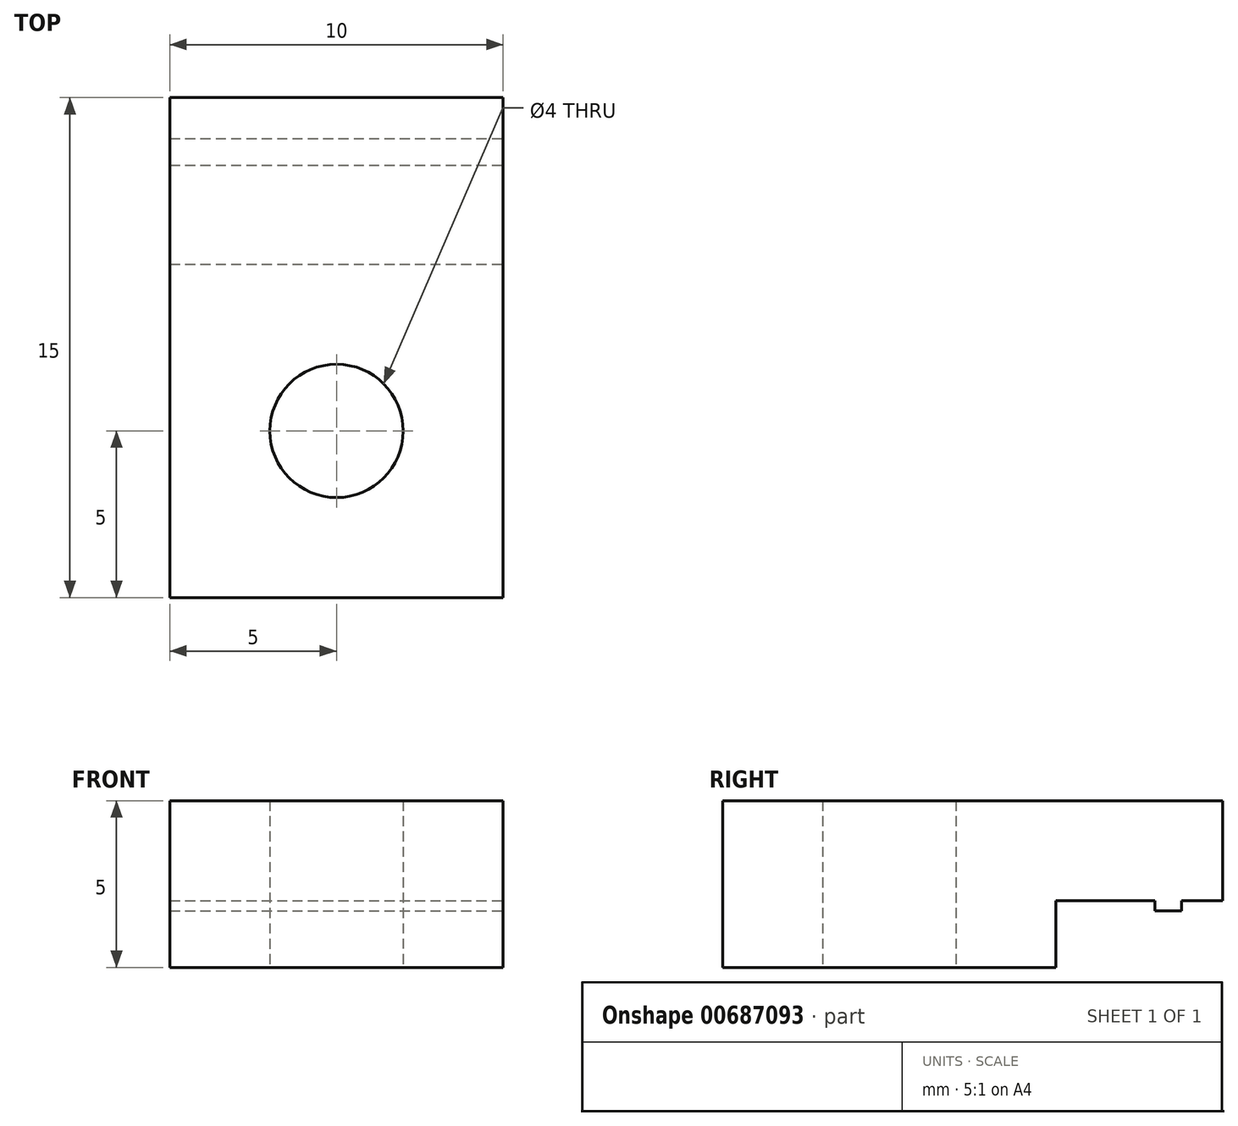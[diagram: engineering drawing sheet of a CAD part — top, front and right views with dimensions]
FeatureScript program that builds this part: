
annotation { "Feature Type Name" : "Feature", "Feature Type Description" : "" }
export const myFeature = defineFeature(function(context is Context, id is Id, definition is map)
    precondition{}
    {
        {
            var Q0;
            Q0=qCreatedBy(makeId("Top.planeOp"),FACE);
            var sketch = newSketch(context, id + "F0", { "sketchPlane" : qUnion([Q0])});
            skLineSegment(sketch, "E0.bottom", {"start": v(0, 0) * mm, "end": v(10, 0) * mm});
            skLineSegment(sketch, "E0.top", {"start": v(0, 15) * mm, "end": v(10, 15) * mm});
            skLineSegment(sketch, "E0.left", {"start": v(0, 0) * mm, "end": v(0, 15) * mm});
            skLineSegment(sketch, "E0.right", {"start": v(10, 0) * mm, "end": v(10, 15) * mm});
            skSolve(sketch);
        }
        {
            var Q0;
            Q0 = qSketchRegion(id + "F0", true);
            extrude(context, id + "F1", {"entities" : qUnion([Q0]), "depth" : 5 * mm, "offsetDistance" : 25 * mm});
        }
        {
            var Q0;
            Q0=makeQuery(id+"F1.opExtrude","SWEPT_FACE",FACE,{"disambiguationData":[OSD([sQuery(id+"F0.wireOp",EDGE,"E0.right")])]});
            var sketch = newSketch(context, id + "F2", { "sketchPlane" : qUnion([Q0])});
            skLineSegment(sketch, "E1", {"start": v(10, 0) * mm, "end": v(10, 2) * mm});
            skLineSegment(sketch, "E2", {"start": v(10, 2) * mm, "end": v(15, 2) * mm});
            skLineSegment(sketch, "E3", {"start": v(15, 2) * mm, "end": v(15, 0) * mm});
            skLineSegment(sketch, "E4", {"start": v(15, 0) * mm, "end": v(10, 0) * mm});
            skSolve(sketch);
        }
        {
            var Q0;
            Q0 = qSketchRegion(id + "F2", true);
            extrude(context, id + "F3", {"entities" : qUnion([Q0]), "operationType" : NewBodyOperationType.REMOVE, "oppositeDirection" : true, "depth" : 25 * mm, "offsetDistance" : 25 * mm});
        }
        {
            var Q0;
            Q0=makeQuery(id+"F1.opExtrude","CAP_FACE",FACE,{"disambiguationData":[OSD([sQuery(id+"F0.wireOp",EDGE,"E0.bottom"),sQuery(id+"F0.wireOp",EDGE,"E0.top"),sQuery(id+"F0.wireOp",EDGE,"E0.left"),sQuery(id+"F0.wireOp",EDGE,"E0.right")])],"isStart":true});
            var sketch = newSketch(context, id + "F4", { "sketchPlane" : qUnion([Q0])});
            skCircle(sketch, "E5", {"center": v(5, -5) * mm, "radius": 2 * mm});
            skPoint(sketch, "E5.centerSnap0", {"position": v(0, -5) * mm});
            skPoint(sketch, "E5.centerSnap1", {"position": v(5, 0) * mm});
            skSolve(sketch);
        }
        {
            var Q0;
            Q0 = qSketchRegion(id + "F4", true);
            extrude(context, id + "F5", {"entities" : qUnion([Q0]), "operationType" : NewBodyOperationType.REMOVE, "oppositeDirection" : true, "depth" : 25 * mm, "offsetDistance" : 25 * mm});
        }
        {
            var Q0;
            Q0=makeQuery(id+"F3.boolean.opBoolean","COPY",FACE,{"derivedFrom":makeQuery(id+"F3.opExtrude","SWEPT_FACE",FACE,{"disambiguationData":[OSD([sQuery(id+"F2.wireOp",EDGE,"E2")])]})});
            var sketch = newSketch(context, id + "F6", { "sketchPlane" : qUnion([Q0])});
            skLineSegment(sketch, "E6.bottom", {"start": v(0, -12.98) * mm, "end": v(10, -12.98) * mm});
            skLineSegment(sketch, "E6.top", {"start": v(0, -13.77) * mm, "end": v(10, -13.77) * mm});
            skLineSegment(sketch, "E6.left", {"start": v(0, -12.98) * mm, "end": v(0, -13.77) * mm});
            skLineSegment(sketch, "E6.right", {"start": v(10, -12.98) * mm, "end": v(10, -13.77) * mm});
            skSolve(sketch);
        }
        {
            var Q0;
            Q0 = qSketchRegion(id + "F6", true);
            extrude(context, id + "F7", {"entities" : qUnion([Q0]), "operationType" : NewBodyOperationType.ADD, "depth" : .3 * mm, "offsetDistance" : 25 * mm});
        }
    });
